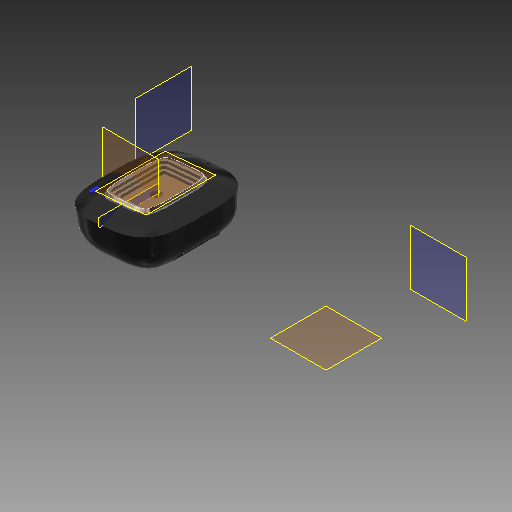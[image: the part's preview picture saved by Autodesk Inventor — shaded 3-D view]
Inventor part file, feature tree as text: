
AUTODESK INVENTOR PART (.ipt)
format: ipt  version: 2018 (Build 220112000, 112)  size: 1,796,608 bytes
history: native  units: mm
features: sketch x18, extrude x13, plane x12, fillet x6, sweep x5, other x5, thicken_offset x4, mirror x3, projected_geometry x3
ambient origin geometry x8: Origin, YZ Plane, XZ Plane, XY Plane, X Axis, Y Axis, Z Axis, Center Point
bodies: Body1 (feature_tree), Body2 (feature_tree), Body3 (feature_tree), Body4 (feature_tree), Body5 (feature_tree)
feature tree (69):
  sketch  "Sketch1"  dims[d0=109.0mm d1=44.5mm d189=90.0deg]
  plane  "Work Plane8"
  plane  "Work Plane7"
  sketch  "Sketch3"  dims[d190=3.0mm d193=0.0mm d194=0.0mm]
  plane  "Work Plane6"
  plane  "Work Plane1"
  sketch  "Sketch5"  dims[d201=0.5mm d202=0.5mm]
  plane  "Work Plane2"
  sketch  "Sketch6"  dims[d204=0.5mm d205=0.2mm]
  plane  "Work Plane5"
  sketch  "Sketch8"  dims[d210=15.0mm d211=-0.872665mm d212=10.0mm]
  mirror  "Mirror1"
  thicken_offset  "Thicken1"
  thicken_offset  "Thicken2"
  mirror  "Mirror3"
  thicken_offset  "Thicken4"
  thicken_offset  "Thicken5"
  extrude  "Extrusion6"  Depth=44.5mm
  fillet  "Fillet1"  [1 undecoded]
  sketch  "Sketch12"  dims[d220=5.0mm d221=0.0mm d224=-1.0mm]
  plane  "Work Plane9"
  sweep  "Sweep1"
  mirror  "Mirror4"
  plane  "Work Plane11"
  extrude  "Extrusion9"  Depth=0.5mm
  plane  "Work Plane13"
  extrude  "Extrusion10"  Depth=0.2mm
  plane  "Work Plane14"
  extrude  "Extrusion11"  Depth=10.0mm
  plane  "Work Plane15"
  extrude  "Extrusion12"  [1 undecoded]
  plane  "Work Plane16"
  sketch  "Sketch20"  dims[d242=1.0mm d243=1.0mm]
  extrude  "Extrusion13"  [1 undecoded]
  extrude  "Extrusion15"  Depth=11.0mm
  sketch  "Sketch21"  dims[d245=1.0mm d246=1.0mm d247=1.0mm d248=0.0mm d249=0.0mm]
  extrude  "Extrusion16"  Depth=8.0mm
  fillet  "Fillet2"  Radius=2.0mm
  sketch  "Sketch22"  dims[d250=3.0mm d251=0.0mm d255=2.75mm d256=0.0mm]
  extrude  "Extrusion17"  [1 undecoded]
  extrude  "Extrusion18"  Depth=6.0mm TaperAngle=0.0deg
  fillet  "Fillet3"  [1 undecoded]
  extrude  "Extrusion19"  Depth=1.0mm
  fillet  "Fillet4"  Radius=1.0mm
  extrude  "Extrusion20"  Depth=1.0mm
  extrude  "Extrusion21"  Depth=1.0mm
  fillet  "Fillet5"  Radius=1.0mm
  fillet  "Fillet6"  [1 undecoded]
  other  "Image4"
  other  "Srf3"
  other  "Srf4"
  other  "Srf7"
  other  "Srf8"
  sketch  "Sketch11"  dims[d213=0.0mm d214=0.0mm d219=-0.5mm]
  sketch  "Sketch13"  dims[d225=22.0mm d226=11.0mm]
  sketch  "Sketch15"  dims[d227=16.0mm d228=8.0mm d229=2.0mm]
  projected_geometry  "Projected Loop7"
  sketch  "Sketch17"  dims[d230=1.0mm d231=0.0mm d232=-1.0mm]
  sketch  "Sketch18"  dims[d233=1.0mm d234=6.0mm d235=0.0mm d236=-1.0mm]
  sketch  "Sketch19"  dims[d237=1.0mm d240=1.0mm d241=1.0mm]
  sketch  "Sketch23"  dims[d257=2.0mm d258=0.0mm d259=0.1mm]
  sketch  "Sketch24"  dims[d260=2.1mm d261=0.0mm d262=2.75mm d263=0.0mm]
  sketch  "Sketch25"  dims[d264=0.1mm d265=1.5mm d266=0.0mm d267=0.5mm d268=10.0mm d269=0.0mm d270=5.0mm d271=5.0mm d272=0.0mm d273=3.0mm d274=0.5mm d275=15.0mm d276=14.0mm]
  projected_geometry  "Projected Loop10"
  sweep  "SweepSrf1"
  sweep  "SweepSrf2"
  sweep  "SweepSrf5"
  sweep  "SweepSrf6"
  projected_geometry  "Project Cut Edges1"
note: 6 required parameter values undecoded (feature->parameter linkage not recoverable at this tier; creation-order binding heuristic only, values carry confidence <= 0.55)
